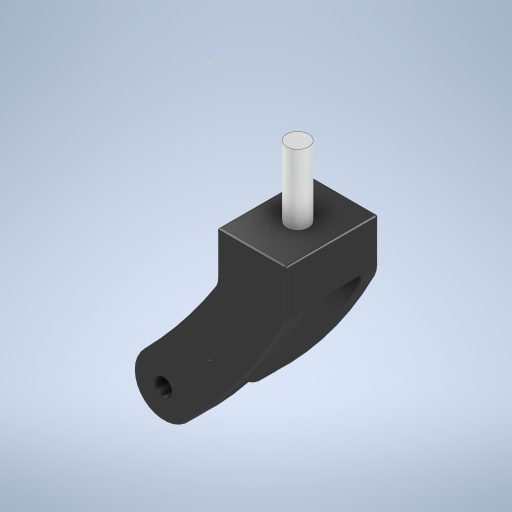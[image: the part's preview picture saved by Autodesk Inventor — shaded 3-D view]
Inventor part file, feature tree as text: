
AUTODESK INVENTOR PART (.ipt)
format: ipt  version: 2023 (Build 270158000, 158)  size: 384,000 bytes
history: native  units: in
note: dims shown in document units (in); Inventor stores cm internally (conversion verified against a paired STEP export)
features: fillet x8, sketch x7, extrude x4, other x1
ambient origin geometry x8: Origin, YZ Plane, XZ Plane, XY Plane, X Axis, Y Axis, Z Axis, Center Point
bodies: Solid1 (feature_tree)
feature tree (20):
  sketch  "Sketch1"  dims[d2=1.0236in d3=0.5906in d6=2.3622in d8=2.9921in]
  sketch  "Sketch2"  dims[d10=0.0in d11=3.937in]
  other  "Work Point1"
  sketch  "Sketch3"  dims[d12=1.6535in d13=3.1496in d14=0.0in d15=0.7874in d16=0.5906in d17=0.5906in d18=0.5906in d19=0.3937in d20=0.0in d21=0.75in]
  extrude  "Extrusion1"  Depth=0.5906in
  fillet  "Fillet1"  Radius=2.3622in
  fillet  "Fillet2"  Radius=2.9921in
  extrude  "Extrusion2"  Depth=3.937in
  extrude  "Extrusion3"  Depth=0.3937in TaperAngle=0.0deg
  fillet  "Fillet3"  Radius=0.7874in
  fillet  "Fillet4"  Radius=0.5906in
  fillet  "Fillet5"  Radius=0.5906in
  fillet  "Fillet6"  Radius=0.5906in
  fillet  "Fillet7"  Radius=0.3937in
  fillet  "Fillet8"  Radius=0.75in
  sketch  "Sketch6"  dims[d26=0.0787in]
  extrude  "Extrusion4"  Depth=0.0787in
  sketch  "Sketch4"  dims[d22=3.1496in d23=0.0in d24=0.0787in]
  sketch  "Sketch5"  dims[d25=0.0787in]
  sketch  "Sketch7"  dims[d27=0.0787in d28=0.0787in d29=0.0787in d30=0.7677in d31=0.0in d32=0.0in d33=0.0in d34=0.0197in d35=0.0344in]
